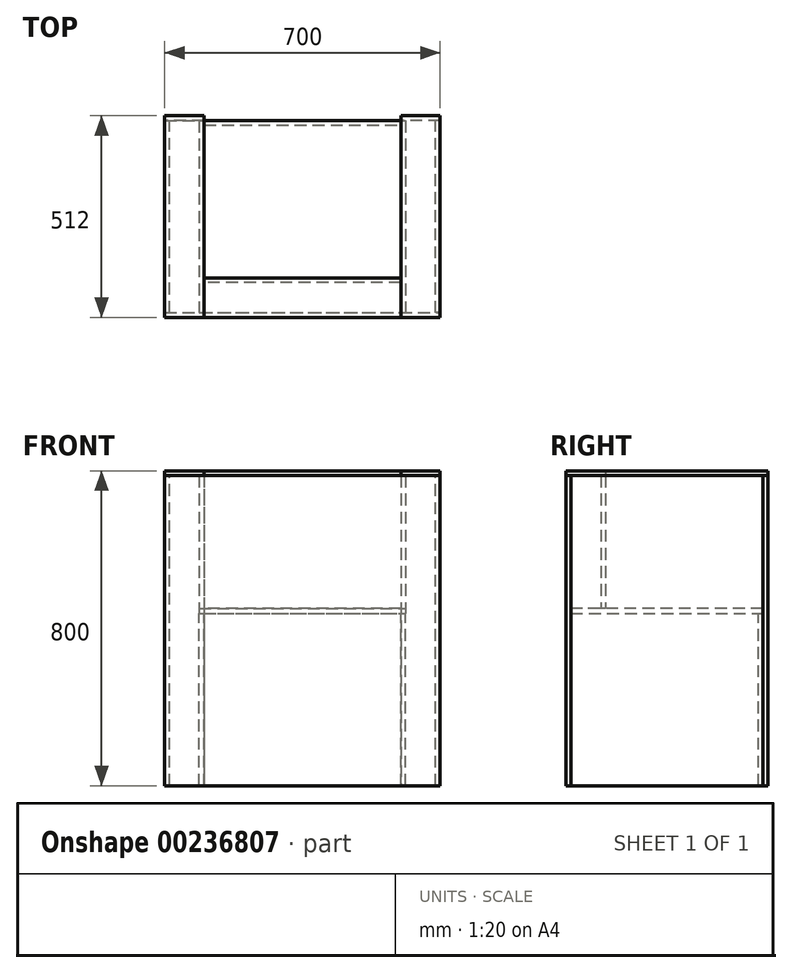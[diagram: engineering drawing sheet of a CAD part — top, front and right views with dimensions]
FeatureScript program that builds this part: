
annotation { "Feature Type Name" : "Feature", "Feature Type Description" : "" }
export const myFeature = defineFeature(function(context is Context, id is Id, definition is map)
    precondition{}
    {
        {
            var Q0;
            Q0=qCreatedBy(makeId("Top.planeOp"),FACE);
            var sketch = newSketch(context, id + "F0", { "sketchPlane" : qUnion([Q0])});
            skLineSegment(sketch, "E0.bottom", {"start": v(-262, 244) * mm, "end": v(262, 244) * mm});
            skLineSegment(sketch, "E0.top", {"start": v(-262, -244) * mm, "end": v(262, -244) * mm});
            skLineSegment(sketch, "E0.left", {"start": v(-262, 244) * mm, "end": v(-262, -244) * mm});
            skLineSegment(sketch, "E0.right", {"start": v(262, 244) * mm, "end": v(262, -244) * mm});
            skPoint(sketch, "E0.middle", {"position": v(0, 0) * mm});
            skSolve(sketch);
        }
        {
            var Q0;
            Q0 = qSketchRegion(id + "F0", true);
            extrude(context, id + "F1", {"entities" : qUnion([Q0]), "depth" : 12 * mm});
        }
        {
            var Q0;
            Q0=makeQuery(id+"F1.opExtrude","CAP_FACE",FACE,{"disambiguationData":[OSD([sQuery(id+"F0.wireOp",EDGE,"E0.bottom"),sQuery(id+"F0.wireOp",EDGE,"E0.top"),sQuery(id+"F0.wireOp",EDGE,"E0.left"),sQuery(id+"F0.wireOp",EDGE,"E0.right")])],"isStart":true});
            var sketch = newSketch(context, id + "F2", { "sketchPlane" : qUnion([Q0])});
            skLineSegment(sketch, "E1.bottom", {"start": v(-262, 244) * mm, "end": v(-250, 244) * mm});
            skLineSegment(sketch, "E1.top", {"start": v(-262, -244) * mm, "end": v(-250, -244) * mm});
            skLineSegment(sketch, "E1.left", {"start": v(-262, 244) * mm, "end": v(-262, -244) * mm});
            skLineSegment(sketch, "E1.right", {"start": v(-250, 244) * mm, "end": v(-250, -244) * mm});
            skLineSegment(sketch, "E2.bottom", {"start": v(262, 244) * mm, "end": v(250, 244) * mm});
            skLineSegment(sketch, "E2.top", {"start": v(262, -244) * mm, "end": v(250, -244) * mm});
            skLineSegment(sketch, "E2.left", {"start": v(262, 244) * mm, "end": v(262, -244) * mm});
            skLineSegment(sketch, "E2.right", {"start": v(250, 244) * mm, "end": v(250, -244) * mm});
            skLineSegment(sketch, "E3.bottom", {"start": v(-250, -244) * mm, "end": v(250, -244) * mm});
            skLineSegment(sketch, "E3.top", {"start": v(-250, -232) * mm, "end": v(250, -232) * mm});
            skLineSegment(sketch, "E3.left", {"start": v(-250, -244) * mm, "end": v(-250, -232) * mm});
            skLineSegment(sketch, "E3.right", {"start": v(250, -244) * mm, "end": v(250, -232) * mm});
            skSolve(sketch);
        }
        {
            var Q0;
            Q0=makeQuery(id+"F2.imprint","IMPRINT",FACE,{"disambiguationData":[TD([[makeQuery(id+"F2.imprint","IMPRINT",EDGE,{"derivedFrom":sQuery(id+"F2.wireOp",EDGE,"E3.bottom")}),1.0]])]});
            extrude(context, id + "F3", {"entities" : qUnion([Q0]), "depth" : 438 * mm});
        }
        {
            var Q0;
            Q0=makeQuery(id+"F2.imprint","IMPRINT",FACE,{"disambiguationData":[TD([[makeQuery(id+"F2.imprint","IMPRINT",EDGE,{"derivedFrom":sQuery(id+"F2.wireOp",EDGE,"E1.bottom")}),-1.0]])]});
            var Q1;
            {var subQ1=sQuery(id+"F2.wireOp",EDGE,"E1.top");Q1=makeQuery(id+"F2.imprint","IMPRINT",FACE,{"disambiguationData":[TD([[makeQuery(id+"F2.imprint","IMPRINT",EDGE,{"derivedFrom":subQ1}),1.0]])]});}
            extrude(context, id + "F4", {"entities" : qUnion([Q0, Q1]), "depth" : 438 * mm});
        }
        {
            var Q0;
            {var subQ0=sQuery(id+"F2.wireOp",EDGE,"E2.bottom");Q0=makeQuery(id+"F2.imprint","IMPRINT",FACE,{"disambiguationData":[TD([[makeQuery(id+"F2.imprint","IMPRINT",EDGE,{"derivedFrom":subQ0}),1.0]])]});}
            var Q1;
            {var subQ5=sQuery(id+"F2.wireOp",EDGE,"E2.top");Q1=makeQuery(id+"F2.imprint","IMPRINT",FACE,{"disambiguationData":[TD([[makeQuery(id+"F2.imprint","IMPRINT",EDGE,{"derivedFrom":subQ5}),1.0]])]});}
            extrude(context, id + "F5", {"entities" : qUnion([Q0, Q1]), "depth" : 438 * mm});
        }
        {
            var Q0;
            Q0=makeQuery(id+"F1.opExtrude","CAP_FACE",FACE,{"disambiguationData":[OSD([sQuery(id+"F0.wireOp",EDGE,"E0.bottom"),sQuery(id+"F0.wireOp",EDGE,"E0.top"),sQuery(id+"F0.wireOp",EDGE,"E0.left"),sQuery(id+"F0.wireOp",EDGE,"E0.right")])],"isStart":false});
            var sketch = newSketch(context, id + "F6", { "sketchPlane" : qUnion([Q0])});
            skLineSegment(sketch, "E4.bottom", {"start": v(262, 244) * mm, "end": v(250, 244) * mm});
            skLineSegment(sketch, "E4.top", {"start": v(262, -244) * mm, "end": v(250, -244) * mm});
            skLineSegment(sketch, "E4.left", {"start": v(262, 244) * mm, "end": v(262, -244) * mm});
            skLineSegment(sketch, "E4.right", {"start": v(250, 244) * mm, "end": v(250, -244) * mm});
            skLineSegment(sketch, "E5.bottom", {"start": v(-262, 244) * mm, "end": v(-250, 244) * mm});
            skLineSegment(sketch, "E5.top", {"start": v(-262, -244) * mm, "end": v(-250, -244) * mm});
            skLineSegment(sketch, "E5.left", {"start": v(-262, 244) * mm, "end": v(-262, -244) * mm});
            skLineSegment(sketch, "E5.right", {"start": v(-250, 244) * mm, "end": v(-250, -244) * mm});
            skLineSegment(sketch, "E6.bottom", {"start": v(250, -168) * mm, "end": v(-250, -168) * mm});
            skLineSegment(sketch, "E6.top", {"start": v(250, -156) * mm, "end": v(-250, -156) * mm});
            skLineSegment(sketch, "E6.left", {"start": v(250, -168) * mm, "end": v(250, -156) * mm});
            skLineSegment(sketch, "E6.right", {"start": v(-250, -168) * mm, "end": v(-250, -156) * mm});
            skSolve(sketch);
        }
        {
            var Q0;
            Q0=makeQuery(id+"F6.imprint","IMPRINT",FACE,{"disambiguationData":[TD([[makeQuery(id+"F6.imprint","IMPRINT",EDGE,{"derivedFrom":sQuery(id+"F6.wireOp",EDGE,"E4.bottom")}),-1.0]])]});
            extrude(context, id + "F7", {"entities" : qUnion([Q0]), "depth" : 338 * mm});
        }
        {
            var Q0;
            Q0=makeQuery(id+"F6.imprint","IMPRINT",FACE,{"disambiguationData":[TD([[makeQuery(id+"F6.imprint","IMPRINT",EDGE,{"derivedFrom":sQuery(id+"F6.wireOp",EDGE,"E5.bottom")}),-1.0]])]});
            extrude(context, id + "F8", {"entities" : qUnion([Q0]), "depth" : 338 * mm});
        }
        {
            var Q0;
            Q0=makeQuery(id+"F6.imprint","IMPRINT",FACE,{"disambiguationData":[TD([[makeQuery(id+"F6.imprint","IMPRINT",EDGE,{"derivedFrom":sQuery(id+"F6.wireOp",EDGE,"E6.bottom")}),-1.0]])]});
            extrude(context, id + "F9", {"entities" : qUnion([Q0]), "depth" : 338 * mm});
        }
        {
            var Q0;
            Q0=makeQuery(id+"F8.opExtrude","SWEPT_FACE",FACE,{"disambiguationData":[OSD([sQuery(id+"F6.wireOp",EDGE,"E5.bottom")])]});
            var sketch = newSketch(context, id + "F10", { "sketchPlane" : qUnion([Q0])});
            skLineSegment(sketch, "E7.bottom", {"start": v(250, 350) * mm, "end": v(350, 350) * mm});
            skLineSegment(sketch, "E7.top", {"start": v(250, -438) * mm, "end": v(350, -438) * mm});
            skLineSegment(sketch, "E7.left", {"start": v(250, 350) * mm, "end": v(250, -438) * mm});
            skLineSegment(sketch, "E7.right", {"start": v(350, 350) * mm, "end": v(350, -438) * mm});
            skLineSegment(sketch, "E8.bottom", {"start": v(-350, 350) * mm, "end": v(-250, 350) * mm});
            skLineSegment(sketch, "E8.top", {"start": v(-350, -438) * mm, "end": v(-250, -438) * mm});
            skLineSegment(sketch, "E8.left", {"start": v(-350, 350) * mm, "end": v(-350, -438) * mm});
            skLineSegment(sketch, "E8.right", {"start": v(-250, 350) * mm, "end": v(-250, -438) * mm});
            skSolve(sketch);
        }
        {
            var Q0;
            Q0=makeQuery(id+"F10.imprint","IMPRINT",FACE,{"disambiguationData":[TD([[makeQuery(id+"F10.imprint","IMPRINT",EDGE,{"derivedFrom":sQuery(id+"F10.wireOp",EDGE,"E8.bottom")}),-1.0]])]});
            extrude(context, id + "F11", {"entities" : qUnion([Q0]), "depth" : 12 * mm});
        }
        {
            var Q0;
            {var subQ1=sQuery(id+"F6.wireOp",EDGE,"E5.bottom");var subQ5=makeQuery(id+"F8.opExtrude","CAP_EDGE",EDGE,{"disambiguationData":[OSD([subQ1])],"isStart":true});Q0=makeQuery(id+"F10.imprint","IMPRINT",FACE,{"disambiguationData":[TD([[makeQuery(id+"F10.imprint","IMPRINT",EDGE,{"derivedFrom":subQ5}),-1.0]])]});}
            var Q1;
            {var subQ1=sQuery(id+"F10.wireOp",EDGE,"E7.top");Q1=makeQuery(id+"F10.imprint","IMPRINT",FACE,{"disambiguationData":[TD([[makeQuery(id+"F10.imprint","IMPRINT",EDGE,{"derivedFrom":subQ1}),1.0]])]});}
            extrude(context, id + "F12", {"entities" : qUnion([Q0, Q1]), "depth" : 12 * mm});
        }
        {
            var Q0;
            Q0=makeQuery(id+"F12.opExtrude","SWEPT_FACE",FACE,{"disambiguationData":[OSD([sQuery(id+"F10.wireOp",EDGE,"E7.bottom")])]});
            var sketch = newSketch(context, id + "F13", { "sketchPlane" : qUnion([Q0])});
            skLineSegment(sketch, "E9.bottom", {"start": v(-350, 256) * mm, "end": v(-250, 256) * mm});
            skLineSegment(sketch, "E9.top", {"start": v(-350, -256) * mm, "end": v(-250, -256) * mm});
            skLineSegment(sketch, "E9.left", {"start": v(-350, 256) * mm, "end": v(-350, -256) * mm});
            skLineSegment(sketch, "E9.right", {"start": v(-250, 256) * mm, "end": v(-250, -256) * mm});
            skLineSegment(sketch, "E10.bottom", {"start": v(350, 256) * mm, "end": v(250, 256) * mm});
            skLineSegment(sketch, "E10.top", {"start": v(350, -256) * mm, "end": v(250, -256) * mm});
            skLineSegment(sketch, "E10.left", {"start": v(350, 256) * mm, "end": v(350, -256) * mm});
            skLineSegment(sketch, "E10.right", {"start": v(250, 256) * mm, "end": v(250, -256) * mm});
            skSolve(sketch);
        }
        {
            var Q0;
            Q0=makeQuery(id+"F13.imprint","IMPRINT",FACE,{"disambiguationData":[TD([[makeQuery(id+"F13.imprint","IMPRINT",EDGE,{"derivedFrom":sQuery(id+"F13.wireOp",EDGE,"E10.bottom")}),1.0]])]});
            extrude(context, id + "F14", {"entities" : qUnion([Q0]), "depth" : 12 * mm});
        }
        {
            var Q0;
            {var subQ0=sQuery(id+"F13.wireOp",EDGE,"E9.top");Q0=makeQuery(id+"F13.imprint","IMPRINT",FACE,{"disambiguationData":[TD([[makeQuery(id+"F13.imprint","IMPRINT",EDGE,{"derivedFrom":subQ0}),1.0]])]});}
            var Q1;
            {var subQ0=sQuery(id+"F13.wireOp",EDGE,"E9.bottom");Q1=makeQuery(id+"F13.imprint","IMPRINT",FACE,{"disambiguationData":[TD([[makeQuery(id+"F13.imprint","IMPRINT",EDGE,{"derivedFrom":subQ0}),-1.0]])]});}
            extrude(context, id + "F15", {"entities" : qUnion([Q0, Q1]), "operationType" : NewBodyOperationType.ADD, "depth" : 12 * mm});
        }
        {
            var Q0;
            {var subQ0=sQuery(id+"F13.wireOp",EDGE,"E9.top");Q0=makeQuery(id+"F13.imprint","IMPRINT",FACE,{"disambiguationData":[TD([[makeQuery(id+"F13.imprint","IMPRINT",EDGE,{"derivedFrom":subQ0}),1.0]])]});}
            var sketch = newSketch(context, id + "F16", { "sketchPlane" : qUnion([Q0])});
            skLineSegment(sketch, "E11.bottom", {"start": v(-350, -244) * mm, "end": v(-338, -244) * mm});
            skLineSegment(sketch, "E11.top", {"start": v(-350, 244) * mm, "end": v(-338, 244) * mm});
            skLineSegment(sketch, "E11.left", {"start": v(-350, -244) * mm, "end": v(-350, 244) * mm});
            skLineSegment(sketch, "E11.right", {"start": v(-338, -244) * mm, "end": v(-338, 244) * mm});
            skLineSegment(sketch, "E12.bottom", {"start": v(350, -244) * mm, "end": v(338, -244) * mm});
            skLineSegment(sketch, "E12.top", {"start": v(350, 244) * mm, "end": v(338, 244) * mm});
            skLineSegment(sketch, "E12.left", {"start": v(350, -244) * mm, "end": v(350, 244) * mm});
            skLineSegment(sketch, "E12.right", {"start": v(338, -244) * mm, "end": v(338, 244) * mm});
            skSolve(sketch);
        }
        {
            var Q0;
            Q0 = qSketchRegion(id + "F16", true);
            extrude(context, id + "F17", {"entities" : qUnion([Q0]), "oppositeDirection" : true, "depth" : 788 * mm});
        }
        {
            var Q0;
            Q0=makeQuery(id+"F17.opExtrude","SWEPT_FACE",FACE,{"disambiguationData":[OSD([sQuery(id+"F16.wireOp",EDGE,"E11.bottom")])]});
            var sketch = newSketch(context, id + "F18", { "sketchPlane" : qUnion([Q0])});
            skLineSegment(sketch, "E13.bottom", {"start": v(-350, 350) * mm, "end": v(350, 350) * mm});
            skLineSegment(sketch, "E13.top", {"start": v(-350, -438) * mm, "end": v(350, -438) * mm});
            skLineSegment(sketch, "E13.left", {"start": v(-350, 350) * mm, "end": v(-350, -438) * mm});
            skLineSegment(sketch, "E13.right", {"start": v(350, 350) * mm, "end": v(350, -438) * mm});
            skSolve(sketch);
        }
        {
            var Q0;
            Q0 = qSketchRegion(id + "F18", true);
            extrude(context, id + "F19", {"entities" : qUnion([Q0]), "depth" : 12 * mm});
        }
        {
            var Q0;
            Q0=makeQuery(id+"F9.opExtrude","CAP_FACE",FACE,{"disambiguationData":[OSD([sQuery(id+"F6.wireOp",EDGE,"E6.bottom"),sQuery(id+"F6.wireOp",EDGE,"E6.top"),sQuery(id+"F6.wireOp",EDGE,"E6.left"),sQuery(id+"F6.wireOp",EDGE,"E6.right")])],"isStart":false});
            var sketch = newSketch(context, id + "F20", { "sketchPlane" : qUnion([Q0])});
            skLineSegment(sketch, "E14.bottom", {"start": v(-250, -156) * mm, "end": v(250, -156) * mm});
            skLineSegment(sketch, "E14.top", {"start": v(-250, -256) * mm, "end": v(250, -256) * mm});
            skLineSegment(sketch, "E14.left", {"start": v(-250, -156) * mm, "end": v(-250, -256) * mm});
            skLineSegment(sketch, "E14.right", {"start": v(250, -156) * mm, "end": v(250, -256) * mm});
            skSolve(sketch);
        }
        {
            var Q0;
            Q0 = qSketchRegion(id + "F20", true);
            extrude(context, id + "F21", {"entities" : qUnion([Q0]), "depth" : 12 * mm});
        }
    });
